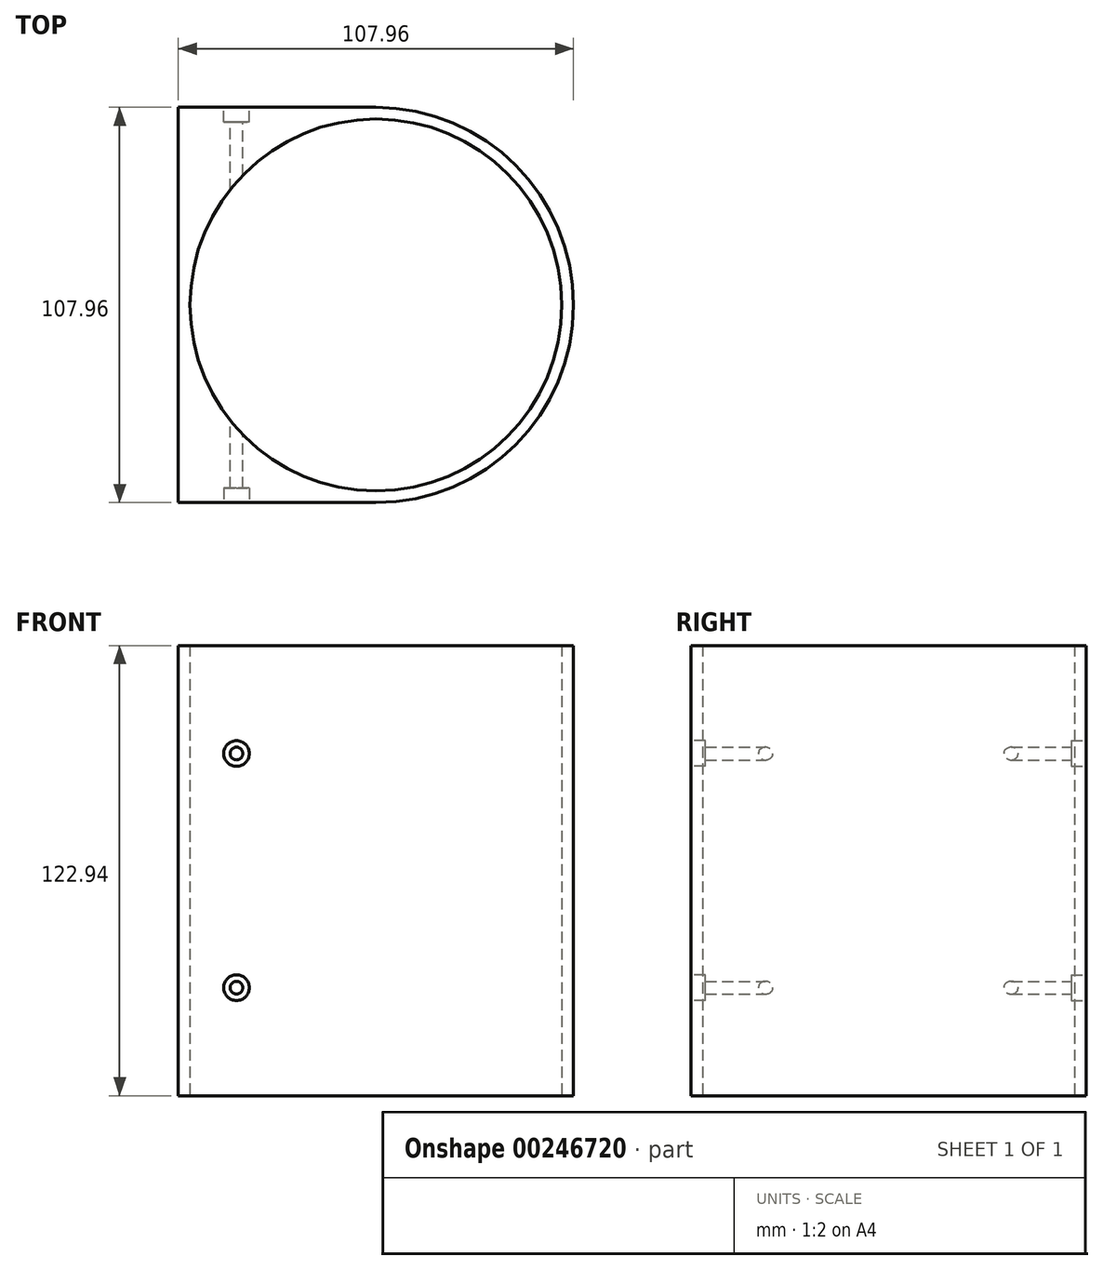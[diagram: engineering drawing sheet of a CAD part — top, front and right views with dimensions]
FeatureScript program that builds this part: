
annotation { "Feature Type Name" : "Feature", "Feature Type Description" : "" }
export const myFeature = defineFeature(function(context is Context, id is Id, definition is map)
    precondition{}
    {
        {
            var Q0;
            Q0=qCreatedBy(makeId("Top.planeOp"),FACE);
            var sketch = newSketch(context, id + "F0", { "sketchPlane" : qUnion([Q0])});
            skArc(sketch, "E0", {"start": v(0, -53.98) * mm, "mid": v(53.98, 0) * mm, "end": v(0, 53.98) * mm});
            skLineSegment(sketch, "E1.bottom", {"start": v(-53.97, 53.98) * mm, "end": v(0, 53.98) * mm});
            skLineSegment(sketch, "E1.top", {"start": v(-53.97, -53.98) * mm, "end": v(0, -53.98) * mm});
            skLineSegment(sketch, "E1.left", {"start": v(-53.98, 53.98) * mm, "end": v(-53.98, -53.98) * mm});
            skCircle(sketch, "E2", {"center": v(0, 0) * mm, "radius": 50.8 * mm});
            skSolve(sketch);
        }
        {
            var Q0;
            Q0 = qSketchRegion(id + "F0", true);
            extrude(context, id + "F1", {"entities" : qUnion([Q0]), "endBound" : BoundingType.SYMMETRIC, "depth" : 122.94 * mm});
        }
        {
            var Q0;
            Q0=makeQuery(id+"F1.opExtrude","SWEPT_FACE",FACE,{"disambiguationData":[OSD([sQuery(id+"F0.wireOp",EDGE,"E1.bottom")])]});
            var sketch = newSketch(context, id + "F2", { "sketchPlane" : qUnion([Q0])});
            skCircle(sketch, "E3", {"center": v(38.1, 31.97) * mm, "radius": 1.74 * mm});
            skCircle(sketch, "E4", {"center": v(38.1, -31.97) * mm, "radius": 1.74 * mm});
            skSolve(sketch);
        }
        {
            var Q0;
            Q0 = qSketchRegion(id + "F2", true);
            extrude(context, id + "F3", {"entities" : qUnion([Q0]), "operationType" : NewBodyOperationType.REMOVE, "oppositeDirection" : true, "depth" : 304.8 * mm});
        }
        {
            var Q0;
            Q0=makeQuery(id+"F1.opExtrude","SWEPT_FACE",FACE,{"disambiguationData":[OSD([sQuery(id+"F0.wireOp",EDGE,"E1.top")])]});
            var sketch = newSketch(context, id + "F4", { "sketchPlane" : qUnion([Q0])});
            skCircle(sketch, "E5", {"center": v(-38.1, 31.97) * mm, "radius": 3.5 * mm});
            skCircle(sketch, "E6", {"center": v(-38.1, -31.97) * mm, "radius": 3.5 * mm});
            skSolve(sketch);
        }
        {
            var Q0;
            Q0 = qSketchRegion(id + "F4", true);
            extrude(context, id + "F5", {"entities" : qUnion([Q0]), "operationType" : NewBodyOperationType.REMOVE, "oppositeDirection" : true, "depth" : 4 * mm});
        }
        {
            var Q0;
            Q0=makeQuery(id+"F1.opExtrude","SWEPT_FACE",FACE,{"disambiguationData":[OSD([sQuery(id+"F0.wireOp",EDGE,"E1.bottom")])]});
            var sketch = newSketch(context, id + "F6", { "sketchPlane" : qUnion([Q0])});
            skCircle(sketch, "E7", {"center": v(38.1, 31.97) * mm, "radius": 3.5 * mm});
            skCircle(sketch, "E8", {"center": v(38.1, -31.97) * mm, "radius": 3.5 * mm});
            skSolve(sketch);
        }
        {
            var Q0;
            Q0 = qSketchRegion(id + "F6", true);
            extrude(context, id + "F7", {"entities" : qUnion([Q0]), "operationType" : NewBodyOperationType.REMOVE, "oppositeDirection" : true, "depth" : 4 * mm});
        }
    });
